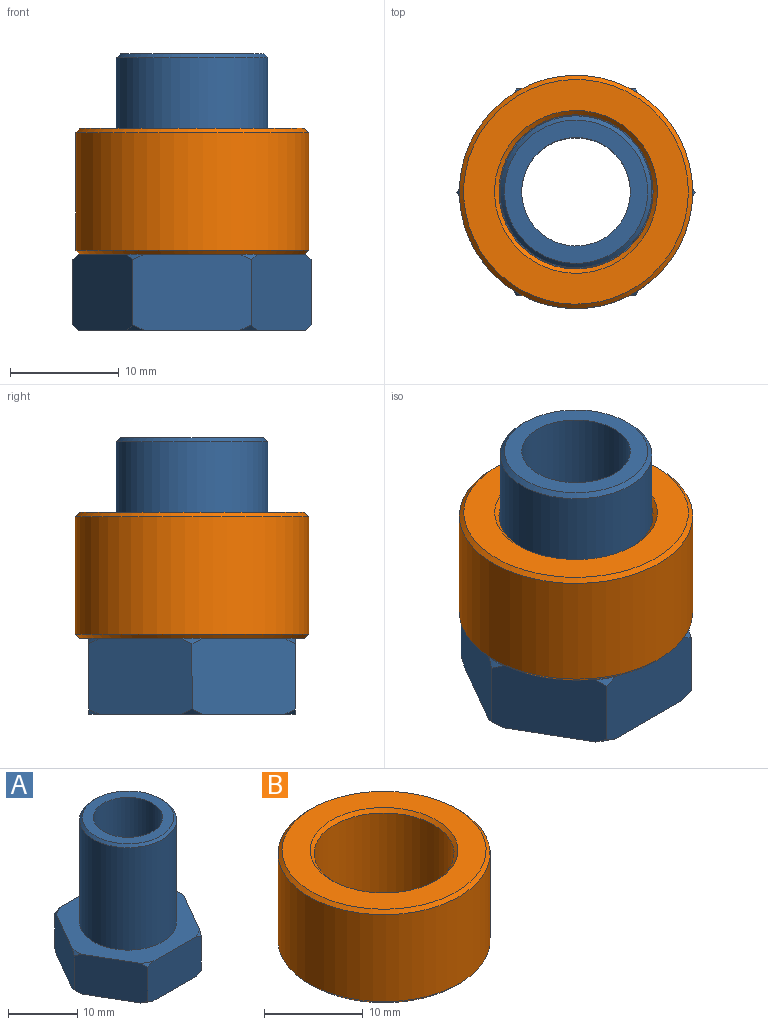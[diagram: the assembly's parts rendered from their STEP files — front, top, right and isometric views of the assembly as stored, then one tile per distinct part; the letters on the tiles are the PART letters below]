
ASSEMBLY  parts=2 mates=1
PART A: 24 faces, bbox 22x19.9x25.5 mm
  f0: plane 9.54x7.04mm, normal (0.87,0.5,0), area 75.7mm2, adj f1,f5,f6,f7,f12,f14,f22,f23
  f1: plane 11.01x7.04mm, normal (0,1,0), area 75.7mm2, adj f0,f2,f6,f7,f20,f21,f22,f23
  f2: plane 9.54x7.04mm, normal (-0.87,0.5,0), area 75.7mm2, adj f1,f3,f6,f7,f18,f19,f20,f21
  f3: plane 9.54x7.04mm, normal (-0.87,-0.5,0), area 75.7mm2, adj f2,f4,f6,f7,f16,f17,f18,f19
  f4: plane 11.01x7.04mm, normal (0,-1,0), area 75.7mm2, adj f3,f5,f6,f7,f13,f15,f16,f17
  f5: plane 9.54x7.04mm, normal (0.87,-0.5,0), area 75.7mm2, adj f0,f4,f6,f7,f12,f13,f14,f15
  f6: plane 20.94x19mm, normal (0,0,1), area 156mm2, adj f0,f1,f2,f3,f4,f5,f8,f14
  f7: plane 20.94x19mm, normal (0,0,-1), area 231.4mm2, adj f0,f1,f2,f3,f4,f5,f10,f12
  f8: cylinder r=7mm len=18.1mm, axis (0,0,-1), area 796.1mm2, adj f6,f11
  f9: plane 13.2x13.2mm, normal (0,0,1), area 58.3mm2, adj f10,f11
  f10: cylinder r=5mm len=25.5mm, axis (0,0,1), area 801.1mm2, adj f7,f9
  f11: cone r=6.6mm half-angle=45deg, axis (0,0,-1), area 24.2mm2, adj f8,f9
  f12: cone r=10.47mm half-angle=45deg, axis (0,0,1), area 0.7mm2, adj f0,f5,f7
  f13: cone r=10.47mm half-angle=45deg, axis (0,0,1), area 0.7mm2, adj f4,f5,f7
  f14: cone r=10.47mm half-angle=45deg, axis (0,0,-1), area 0.7mm2, adj f0,f5,f6
  f15: cone r=10.47mm half-angle=45deg, axis (0,0,-1), area 0.7mm2, adj f4,f5,f6
  f16: cone r=10.47mm half-angle=45deg, axis (0,0,1), area 0.7mm2, adj f3,f4,f7
  f17: cone r=10.47mm half-angle=45deg, axis (0,0,-1), area 0.7mm2, adj f3,f4,f6
  f18: cone r=10.47mm half-angle=45deg, axis (0,0,1), area 0.7mm2, adj f2,f3,f7
  f19: cone r=10.47mm half-angle=45deg, axis (0,0,-1), area 0.7mm2, adj f2,f3,f6
  f20: cone r=10.47mm half-angle=45deg, axis (0,0,1), area 0.7mm2, adj f1,f2,f7
  f21: cone r=10.47mm half-angle=45deg, axis (0,0,-1), area 0.7mm2, adj f1,f2,f6
  f22: cone r=10.47mm half-angle=45deg, axis (0,0,1), area 0.7mm2, adj f0,f1,f7
  f23: cone r=10.47mm half-angle=45deg, axis (0,0,-1), area 0.7mm2, adj f0,f1,f6
PART B: 8 faces, bbox 21.5x21.5x11.6 mm
  f0: cylinder r=7.1mm len=14.2mm, axis (0,0,-1), area 481.8mm2, adj f4,f5
  f1: cylinder r=10.75mm len=21.5mm, axis (0,0,-1), area 729.5mm2, adj f6,f7
  f2: plane 20.7x20.7mm, normal (0,0,1), area 159.8mm2, adj f5,f6
  f3: plane 20.7x20.7mm, normal (0,0,-1), area 159.8mm2, adj f4,f7
  f4: cone r=7.5mm half-angle=45deg, axis (0,0,-1), area 25.9mm2, adj f0,f3
  f5: cone r=7.1mm half-angle=45deg, axis (0,0,1), area 25.9mm2, adj f0,f2
  f6: cone r=10.35mm half-angle=45deg, axis (0,0,-1), area 37.5mm2, adj f1,f2
  f7: cone r=10.75mm half-angle=45deg, axis (0,0,1), area 37.5mm2, adj f1,f3
PLACE A t=(-19.64,-0.89,2.88)mm
PLACE B t=(-19.64,-0.89,9.88)mm
MATE slider A.f8 <-> B.f1  axis (0,0,1) through (-19.64,-0.89,9.88)mm
